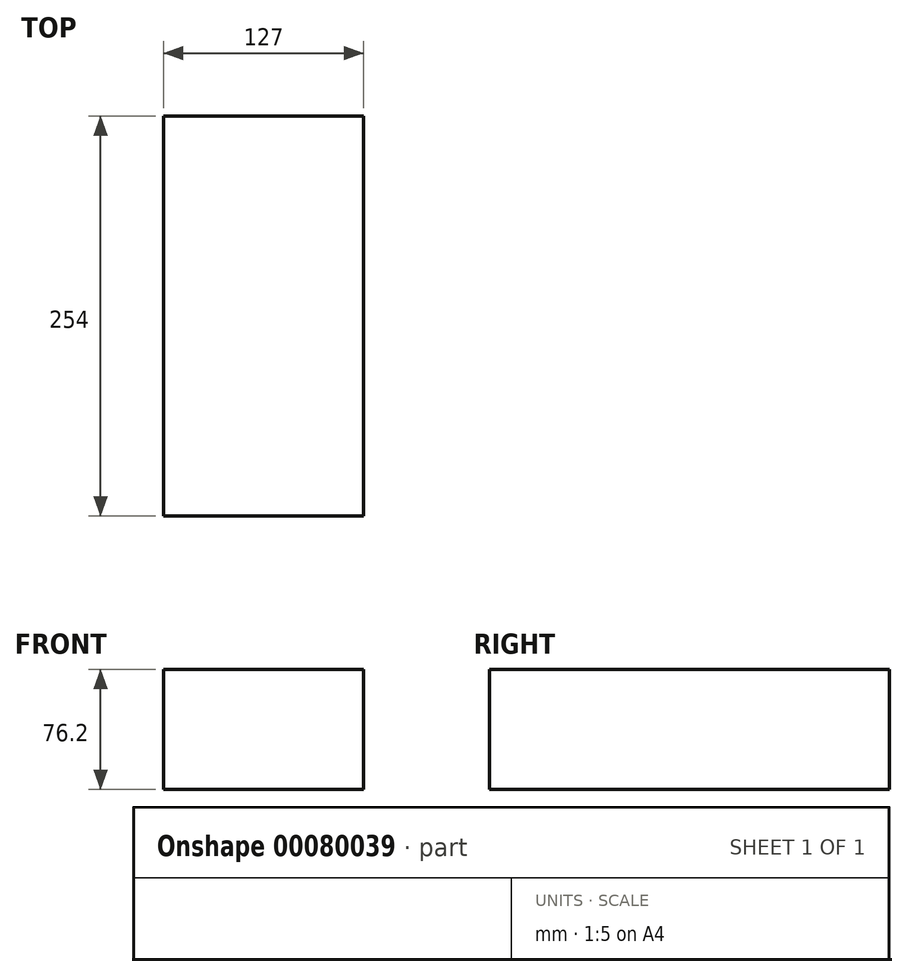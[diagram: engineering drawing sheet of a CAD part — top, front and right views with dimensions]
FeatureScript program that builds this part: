
annotation { "Feature Type Name" : "Feature", "Feature Type Description" : "" }
export const myFeature = defineFeature(function(context is Context, id is Id, definition is map)
    precondition{}
    {
        {
            var Q0;
            Q0=qCreatedBy(makeId("Front.planeOp"),FACE);
            var sketch = newSketch(context, id + "F0", { "sketchPlane" : qUnion([Q0])});
            skLineSegment(sketch, "E0.bottom", {"start": v(63.5, 38.1) * mm, "end": v(-63.5, 38.1) * mm});
            skLineSegment(sketch, "E0.top", {"start": v(63.5, -38.1) * mm, "end": v(-63.5, -38.1) * mm});
            skLineSegment(sketch, "E0.left", {"start": v(63.5, 38.1) * mm, "end": v(63.5, -38.1) * mm});
            skLineSegment(sketch, "E0.right", {"start": v(-63.5, 38.1) * mm, "end": v(-63.5, -38.1) * mm});
            skPoint(sketch, "E0.middle", {"position": v(0, 0) * mm});
            skSolve(sketch);
        }
        {
            var Q0;
            Q0 = qSketchRegion(id + "F0", true);
            extrude(context, id + "F1", {"entities" : qUnion([Q0]), "endBound" : BoundingType.SYMMETRIC, "depth" : 254 * mm});
        }
    });
